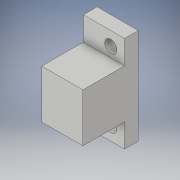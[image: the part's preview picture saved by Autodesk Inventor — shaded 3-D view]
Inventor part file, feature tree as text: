
AUTODESK INVENTOR PART (.ipt)
format: ipt  version: 2019.3 (Build 233278000, 278)  size: 135,168 bytes
history: native  units: mm
features: reference x4, extrude x3, sketch x3, other x3
ambient origin geometry x8: Origin, YZ Plane, XZ Plane, XY Plane, X Axis, Y Axis, Z Axis, Center Point
bodies: Solid1 (feature_tree)
feature tree (13):
  extrude  "Extrusion1"  Depth=30.0mm
  extrude  "Extrusion2"  Depth=5.0mm
  extrude  "Extrusion3"  Depth=35.4mm TaperAngle=0.0deg
  sketch  "Sketch1"  dims[d1=30.0mm d2=60.0mm]
  reference  "Reference1"
  reference  "Reference2"
  reference  "Reference3"
  reference  "Reference4"
  sketch  "Sketch2"  dims[d5=10.0mm d6=0.0mm d7=5.0mm]
  sketch  "Sketch3"  dims[d8=30.4mm d9=0.0mm d18=35.4mm d19=0.0mm d21=25.4mm d22=25.4mm d23=5.0mm d24=5.0mm d26=35.4mm d27=17.3mm d28=10.0mm d29=10.0mm]
  parser-record x1  (decoder bookkeeping rows leaked as tree rows — omitted from the tree; the rows remain in map.json)
  other  "Assembly.iam"
  other  "CameraBracket:1"
note: 1 file-system path scrubbed to <path> (originals preserved in map.json)
